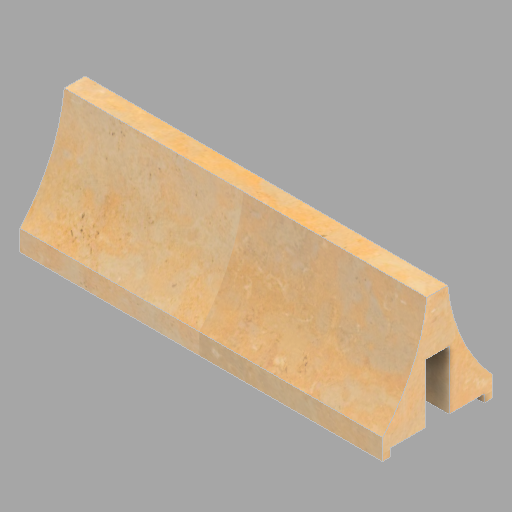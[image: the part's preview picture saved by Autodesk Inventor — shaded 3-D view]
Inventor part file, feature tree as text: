
AUTODESK INVENTOR PART (.ipt)
format: ipt  version: 2022.2 (Build 262287010, 287A)  size: 311,808 bytes
history: native  units: in
note: dims shown in document units (in); Inventor stores cm internally (conversion verified against a paired STEP export)
features: other x1, direct_edit x1, revolve x1
ambient origin geometry x8: Origin, YZ Plane, XZ Plane, XY Plane, X Axis, Y Axis, Z Axis, Center Point
bodies: Solid1 (feature_tree)
feature tree (3):
  other  "North (8)"
  direct_edit  "Direct Edit1"
  revolve  "Rotate1"  [1 undecoded]
note: 1 required parameter value undecoded (feature->parameter linkage not recoverable at this tier; creation-order binding heuristic only, values carry confidence <= 0.55)
